# Revit family: Shower-Valve_Trim-KOHLER-MODULO-K-72816T_1
name_source: partatom
category: Plumbing Fixtures
revit_build: Autodesk Revit 2017 (Build: 20160225_1515(x64)
units: mm (PartAtom-declared; Revit-internal decimal feet)

## family parameters
Cut with Voids When Loaded = No
Host = Face
OmniClass Number = 23.31.25.00
Part Type = Normal
Room Calculation Point = No
Round Connector Dimension = Use Diameter
Shared = No

## types (5) — shared parameters
ADA Compliant = No
Assembly Code = D2010700
CW Connection = Yes
Cold Water Inlet = Cold Water Inlet
Date Modified = 10/09/2020
Default Elevation = 42"
Description = Smart with round in-wall thermostatic shower valve core and classic panel (Philfas handle)
Drain Included = No
Flow Rate = 0 GPM
HW Connection = Yes
Handle Clearance = 3 7/16"
Height = 7 1/16"
Hot Water Inlet = Hot Water Inlet
Length = 4 5/8"
Manufacturer = KOHLER Co.
Master Format 2014 = 22 42 23
Master Format 2014 Name = Residential Showers
Material = Premium Metal Construction
Pressure = 11.00 psi
Product Documentation Link = https://files.kohler.com.cn
Product Name = MODULO
Product Page URL = https://www.kohler.com.cn
Tempered Water Outlet = Tempered Water Outlet
URL = http://www.kohler.com.cn
Vent Connection = No
Waste Connection = No
Waste Water Outlet = Waste Water Outlet
WaterSense Certified = No
Width = 7 1/16"

## per-type parameters (varying)
| type | Finish | Model | Type |
| CP-Polished Chrome | Kohler-Metal-CP-Polished_Chrome | K-72816T-B4-CP | 1 |
| AF-Flange Gold | Kohler-Metal-AF-Flange_Gold | K-72816T-B4-AF | 2 |
| SN-Champagne Gold | Kohler-Metal-SN-Champagne_Gold | K-72816T-B4-SN | 5 |
| BN-Roman Silver | Kohler-Metal-BN-Roman_Silver | K-72816T-B4-BN | 3 |
| BV-Roman Copper | Kohler-Metal-BV-Roman_Copper | K-72816T-B4-BV | 4 |

## geometry (parser evidence)
native form markers: Sweep x5
no freeform markers — native parametric forms only
